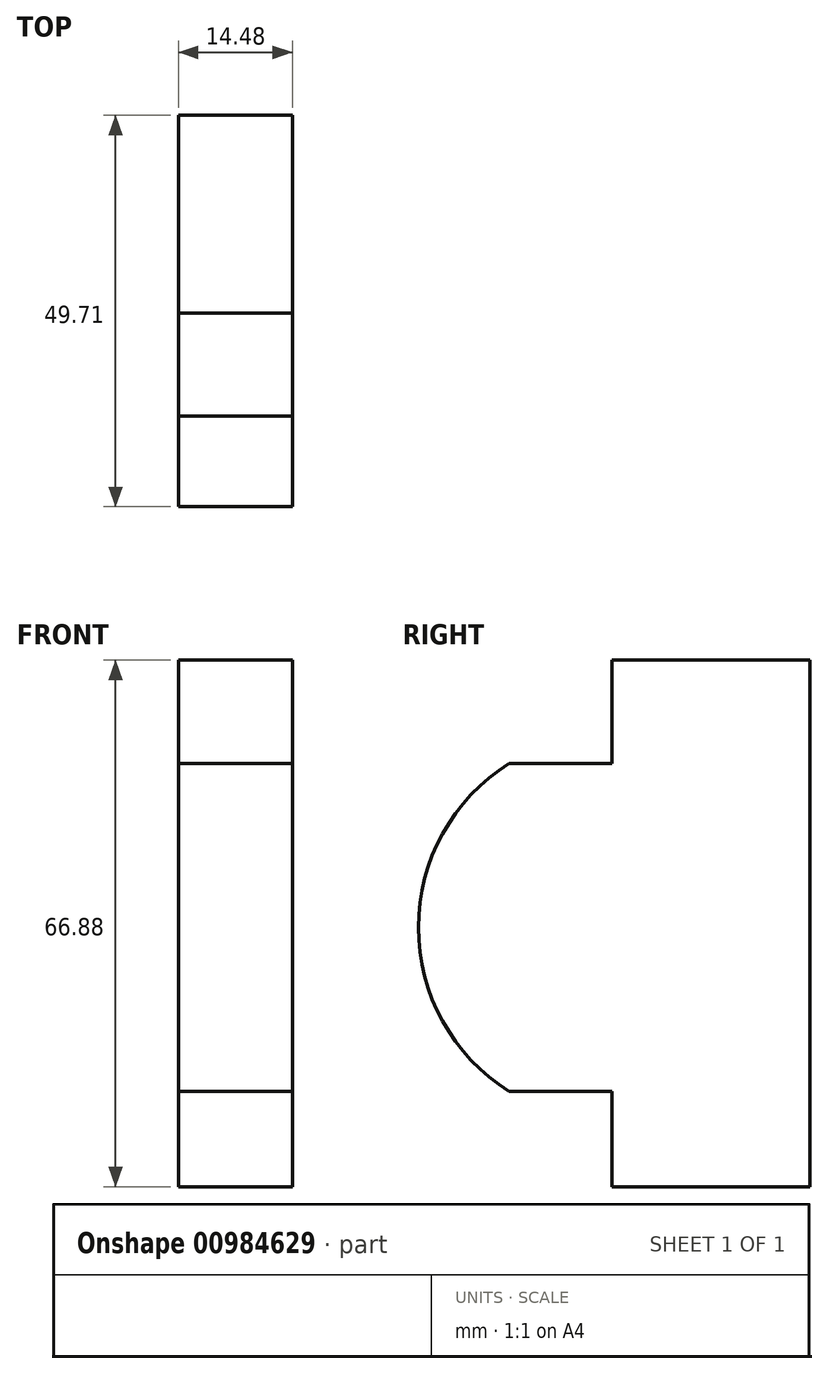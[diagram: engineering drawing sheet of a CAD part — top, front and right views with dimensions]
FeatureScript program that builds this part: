
annotation { "Feature Type Name" : "Feature", "Feature Type Description" : "" }
export const myFeature = defineFeature(function(context is Context, id is Id, definition is map)
    precondition{}
    {
        {
            var Q0;
            Q0=qCreatedBy(makeId("Right.planeOp"),FACE);
            var sketch = newSketch(context, id + "F0", { "sketchPlane" : qUnion([Q0])});
            skLineSegment(sketch, "E0", {"start": v(0, 34.62) * mm, "end": v(-25.12, 34.62) * mm});
            skLineSegment(sketch, "E1", {"start": v(-25.12, 34.62) * mm, "end": v(-25.12, 21.5) * mm});
            skLineSegment(sketch, "E2", {"start": v(-25.12, 21.5) * mm, "end": v(-38.18, 21.5) * mm});
            skArc(sketch, "E3", {"start": v(-38.18, 21.5) * mm, "mid": v(-49.7, 0.67) * mm, "end": v(-38.18, -20.16) * mm});
            skLineSegment(sketch, "E4", {"start": v(-38.18, -20.16) * mm, "end": v(-25.12, -20.16) * mm});
            skLineSegment(sketch, "E5", {"start": v(-25.12, -20.16) * mm, "end": v(-25.12, -32.26) * mm});
            skLineSegment(sketch, "E6", {"start": v(-25.12, -32.26) * mm, "end": v(0, -32.26) * mm});
            skLineSegment(sketch, "E7", {"start": v(0, -32.26) * mm, "end": v(0, 34.62) * mm});
            skSolve(sketch);
        }
        {
            var Q0;
            Q0 = qSketchRegion(id + "F0", true);
            extrude(context, id + "F1", {"entities" : qUnion([Q0]), "depth" : 14.48 * mm, "offsetDistance" : 25.4 * mm});
        }
    });
